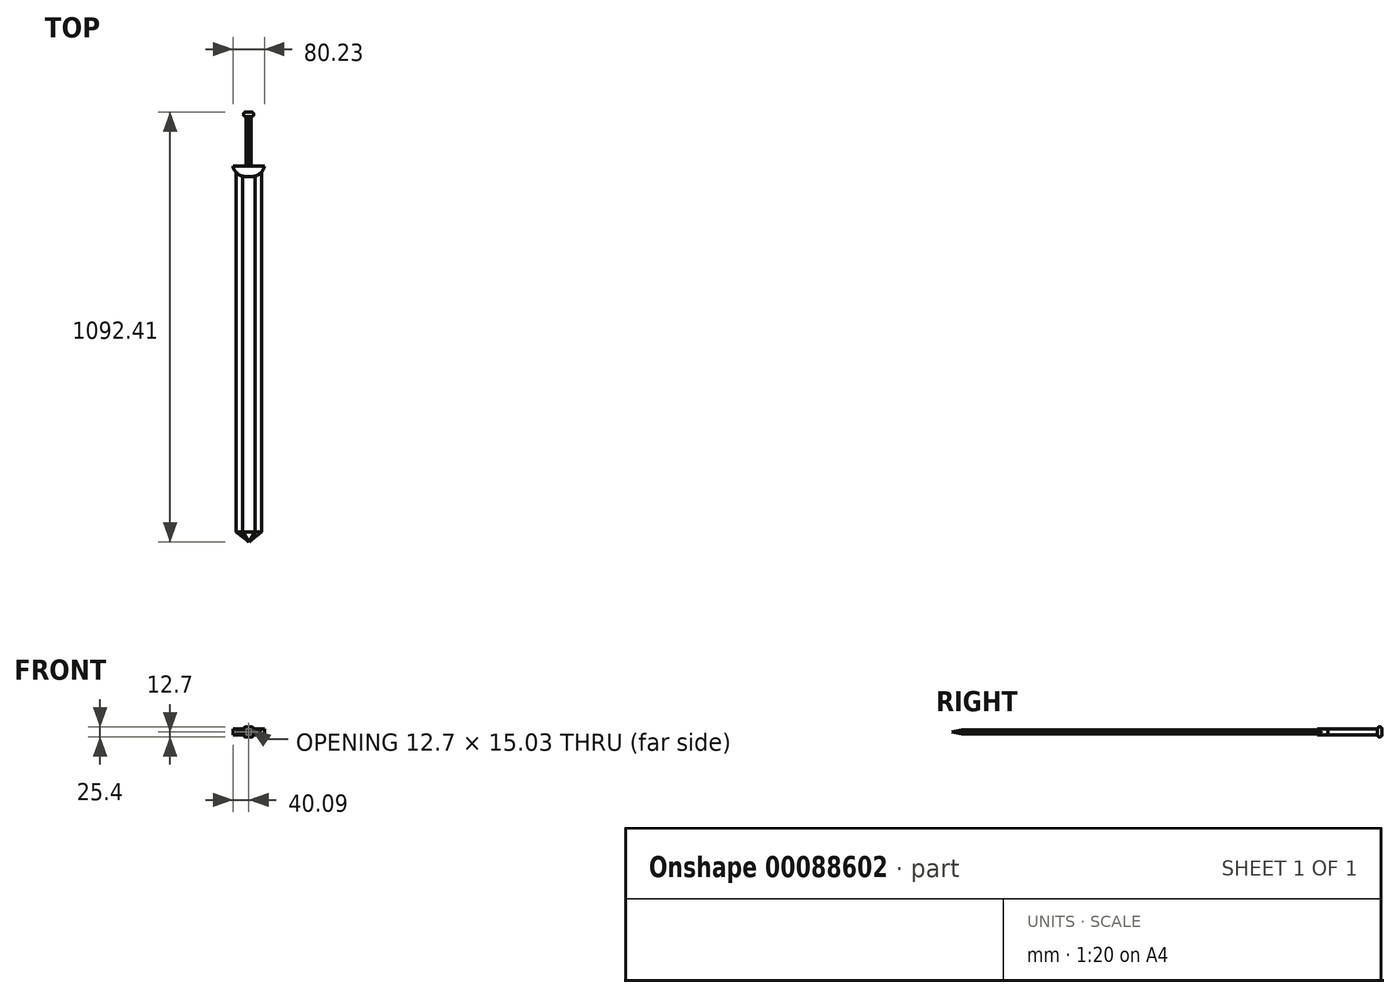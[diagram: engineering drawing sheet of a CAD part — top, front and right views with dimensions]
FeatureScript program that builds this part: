
annotation { "Feature Type Name" : "Feature", "Feature Type Description" : "" }
export const myFeature = defineFeature(function(context is Context, id is Id, definition is map)
    precondition{}
    {
        {
            var Q0;
            Q0=qCreatedBy(makeId("Right.planeOp"),FACE);
            var sketch = newSketch(context, id + "F0", { "sketchPlane" : qUnion([Q0])});
            skLineSegment(sketch, "E0.bottom", {"start": v(0, 0) * mm, "end": v(152.4, 0) * mm});
            skLineSegment(sketch, "E0.top", {"start": v(0, -15.24) * mm, "end": v(152.4, -15.24) * mm});
            skLineSegment(sketch, "E0.left", {"start": v(0, 0) * mm, "end": v(0, -15.24) * mm});
            skLineSegment(sketch, "E0.right", {"start": v(152.4, 0) * mm, "end": v(152.4, -15.24) * mm});
            skSolve(sketch);
        }
        {
            var Q0;
            Q0 = qSketchRegion(id + "F0", true);
            extrude(context, id + "F1", {"entities" : qUnion([Q0]), "depth" : 12.7 * mm});
        }
        {
            var Q0;
            Q0=makeQuery(id+"F1.opExtrude","CAP_EDGE",EDGE,{"disambiguationData":[OSD([sQuery(id+"F0.wireOp",EDGE,"E0.bottom")])],"isStart":true});
            var Q1;
            Q1=makeQuery(id+"F1.opExtrude","CAP_EDGE",EDGE,{"disambiguationData":[OSD([sQuery(id+"F0.wireOp",EDGE,"E0.top")])],"isStart":true});
            var Q2;
            Q2=makeQuery(id+"F1.opExtrude","CAP_EDGE",EDGE,{"disambiguationData":[OSD([sQuery(id+"F0.wireOp",EDGE,"E0.bottom")])],"isStart":false});
            var Q3;
            Q3=makeQuery(id+"F1.opExtrude","CAP_EDGE",EDGE,{"disambiguationData":[OSD([sQuery(id+"F0.wireOp",EDGE,"E0.top")])],"isStart":false});
            fillet(context, id + "F2", {"entities" : qUnion([Q0, Q1, Q2, Q3]), "radius" : 7.62 * mm, "tangentPropagation" : true, "allowEdgeOverflow" : false});
        }
        {
            var Q0;
            Q0=qCreatedBy(makeId("Top.planeOp"),FACE);
            cPlane(context, id + "F3", {"entities" : qUnion([Q0]), "cplaneType" : CPlaneType.OFFSET, "offset" : 7.62 * mm, "oppositeDirection" : true, "width" : 152.4 * mm, "height" : 152.4 * mm});
        }
        {
            var Q0;
            Q0=qCreatedBy(id+"F3.planeOp",FACE);
            var sketch = newSketch(context, id + "F4", { "sketchPlane" : qUnion([Q0])});
            skLineSegment(sketch, "E1.bottom", {"start": v(18.55, 152.06) * mm, "end": v(-6.52, 152.06) * mm});
            skLineSegment(sketch, "E1.top", {"start": v(18.55, 163.8) * mm, "end": v(-6.52, 163.8) * mm});
            skLineSegment(sketch, "E1.left", {"start": v(18.55, 152.06) * mm, "end": v(18.55, 163.8) * mm});
            skLineSegment(sketch, "E1.right", {"start": v(-6.52, 152.06) * mm, "end": v(-6.52, 163.8) * mm});
            skSolve(sketch);
        }
        {
            var Q0;
            Q0 = qSketchRegion(id + "F4", true);
            extrude(context, id + "F5", {"entities" : qUnion([Q0]), "operationType" : NewBodyOperationType.ADD, "depth" : 12.7 * mm, "hasSecondDirection" : true, "secondDirectionOppositeDirection" : true, "secondDirectionDepth" : 12.7 * mm});
        }
        {
            var Q0;
            Q0=qCreatedBy(id+"F3.planeOp",FACE);
            var sketch = newSketch(context, id + "F6", { "sketchPlane" : qUnion([Q0])});
            skArc(sketch, "E2", {"start": v(12.58, -0.66) * mm, "mid": v(34.22, 6.89) * mm, "end": v(46.5, 26.25) * mm});
            skLineSegment(sketch, "E3", {"start": v(12.58, -0.66) * mm, "end": v(0.2, -0.66) * mm});
            skLineSegment(sketch, "E4", {"start": v(6.39, -0.66) * mm, "end": v(6.39, 36.48) * mm});
            skLineSegment(sketch, "E5", {"start": v(46.5, 26.25) * mm, "end": v(6.39, 26.25) * mm});
            skLineSegment(sketch, "E6", {"start": v(6.39, 26.25) * mm, "end": v(-33.74, 26.25) * mm});
            skArc(sketch, "E7", {"start": v(-33.74, 26.25) * mm, "mid": v(-21.46, 6.88) * mm, "end": v(0.2, -0.66) * mm});
            skSolve(sketch);
        }
        {
            var Q0;
            Q0 = qSketchRegion(id + "F6", true);
            extrude(context, id + "F7", {"entities" : qUnion([Q0]), "operationType" : NewBodyOperationType.ADD, "depth" : 7.62 * mm, "hasSecondDirection" : true, "secondDirectionOppositeDirection" : true, "secondDirectionDepth" : 7.62 * mm});
        }
        {
            var Q0;
            Q0=qCreatedBy(id+"F3.planeOp",FACE);
            var sketch = newSketch(context, id + "F8", { "sketchPlane" : qUnion([Q0])});
            skLineSegment(sketch, "E8.bottom", {"start": v(-26.26, 11.18) * mm, "end": v(39.35, 11.18) * mm});
            skLineSegment(sketch, "E8.top", {"start": v(-26.26, -903.22) * mm, "end": v(39.35, -903.22) * mm});
            skLineSegment(sketch, "E8.left", {"start": v(-26.26, 11.18) * mm, "end": v(-26.26, -903.22) * mm});
            skLineSegment(sketch, "E8.right", {"start": v(39.35, 11.18) * mm, "end": v(39.35, -903.22) * mm});
            skSolve(sketch);
        }
        {
            var Q0;
            Q0 = qSketchRegion(id + "F8", true);
            extrude(context, id + "F9", {"entities" : qUnion([Q0]), "operationType" : NewBodyOperationType.ADD, "oppositeDirection" : true, "depth" : 5.08 * mm, "hasSecondDirection" : true, "secondDirectionOppositeDirection" : false, "secondDirectionDepth" : 5.08 * mm});
        }
        {
            var Q0;
            Q0=makeQuery(id+"F9.opExtrude","SWEPT_FACE",FACE,{"disambiguationData":[OSD([sQuery(id+"F8.wireOp",EDGE,"E8.top")])]});
            var sketch = newSketch(context, id + "F10", { "sketchPlane" : qUnion([Q0])});
            skLineSegment(sketch, "E9", {"start": v(-26.26, -7.62) * mm, "end": v(-9.22, -2.54) * mm});
            skLineSegment(sketch, "E10", {"start": v(-26.26, -7.62) * mm, "end": v(-9.22, -12.7) * mm});
            skLineSegment(sketch, "E11", {"start": v(39.35, -7.62) * mm, "end": v(22.3, -2.54) * mm});
            skLineSegment(sketch, "E12", {"start": v(39.35, -7.62) * mm, "end": v(22.3, -12.7) * mm});
            skSolve(sketch);
        }
        {
            var Q0;
            Q0 = qSketchRegion(id + "F10", true);
            var Q1;
            {var subQ0=sQuery(id+"F10.wireOp",EDGE,"E9");Q1=makeQuery(id+"F10.imprint","IMPRINT",FACE,{"disambiguationData":[TD([[makeQuery(id+"F10.imprint","IMPRINT",EDGE,{"derivedFrom":subQ0}),1.0]])]});}
            var Q2;
            {var subQ0=sQuery(id+"F10.wireOp",EDGE,"E10");Q2=makeQuery(id+"F10.imprint","IMPRINT",FACE,{"disambiguationData":[TD([[makeQuery(id+"F10.imprint","IMPRINT",EDGE,{"derivedFrom":subQ0}),-1.0]])]});}
            var Q3;
            {var subQ0=sQuery(id+"F10.wireOp",EDGE,"E12");Q3=makeQuery(id+"F10.imprint","IMPRINT",FACE,{"disambiguationData":[TD([[makeQuery(id+"F10.imprint","IMPRINT",EDGE,{"derivedFrom":subQ0}),1.0]])]});}
            var Q4;
            {var subQ0=sQuery(id+"F10.wireOp",EDGE,"E11");Q4=makeQuery(id+"F10.imprint","IMPRINT",FACE,{"disambiguationData":[TD([[makeQuery(id+"F10.imprint","IMPRINT",EDGE,{"derivedFrom":subQ0}),-1.0]])]});}
            extrude(context, id + "F11", {"entities" : qUnion([Q0, Q1, Q2, Q3, Q4]), "operationType" : NewBodyOperationType.REMOVE, "oppositeDirection" : true, "depth" : 914.4 * mm});
        }
        {
            var Q0;
            Q0=makeQuery(id+"F7.opExtrude","CAP_FACE",FACE,{"disambiguationData":[OSD([sQuery(id+"F6.wireOp",EDGE,"E2"),sQuery(id+"F6.wireOp",EDGE,"E3"),sQuery(id+"F6.wireOp",EDGE,"E5"),sQuery(id+"F6.wireOp",EDGE,"E6"),sQuery(id+"F6.wireOp",EDGE,"E7")])],"isStart":false});
            extrude(context, id + "F12", {"entities" : qUnion([Q0]), "operationType" : NewBodyOperationType.ADD, "oppositeDirection" : true, "depth" : 12.7 * mm});
        }
        {
            var Q0;
            Q0=makeQuery(id+"F9.opExtrude","SWEPT_FACE",FACE,{"disambiguationData":[OSD([sQuery(id+"F8.wireOp",EDGE,"E8.top")])]});
            cPlane(context, id + "F13", {"entities" : qUnion([Q0]), "cplaneType" : CPlaneType.OFFSET, "offset" : 25.4 * mm, "width" : 152.4 * mm, "height" : 152.4 * mm});
        }
        {
            var Q0;
            Q0=qCreatedBy(id+"F13.planeOp",FACE);
            var sketch = newSketch(context, id + "F14", { "sketchPlane" : qUnion([Q0])});
            skPoint(sketch, "E13", {"position": v(6.65, -7.57) * mm});
            skSolve(sketch);
        }
        {
            var Q1;
            Q1=makeQuery(id+"F9.opExtrude","SWEPT_FACE",FACE,{"disambiguationData":[OSD([sQuery(id+"F8.wireOp",EDGE,"E8.top")])]});
            var Q2;
            Q2=sQuery(id+"F14.wireOp",VERTEX,"E13");
            loft(context, id + "F15", {"operationType" : NewBodyOperationType.ADD, "sheetProfilesArray" : [{ "sheetProfileEntities" : qUnion([Q1]) }, { "sheetProfileEntities" : qUnion([Q2]) }]});
        }
        {
            var Q0;
            Q0=makeQuery(id+"F5.opExtrude","SWEPT_FACE",FACE,{"disambiguationData":[OSD([sQuery(id+"F4.wireOp",EDGE,"E1.right")])]});
            var Q1;
            Q1=makeQuery(id+"F5.opExtrude","CAP_FACE",FACE,{"disambiguationData":[OSD([sQuery(id+"F4.wireOp",EDGE,"E1.bottom"),sQuery(id+"F4.wireOp",EDGE,"E1.top"),sQuery(id+"F4.wireOp",EDGE,"E1.left"),sQuery(id+"F4.wireOp",EDGE,"E1.right")])],"isStart":false});
            var Q2;
            Q2=makeQuery(id+"F5.opExtrude","SWEPT_FACE",FACE,{"disambiguationData":[OSD([sQuery(id+"F4.wireOp",EDGE,"E1.left")])]});
            var Q3;
            Q3=makeQuery(id+"F5.opExtrude","CAP_FACE",FACE,{"disambiguationData":[OSD([sQuery(id+"F4.wireOp",EDGE,"E1.bottom"),sQuery(id+"F4.wireOp",EDGE,"E1.top"),sQuery(id+"F4.wireOp",EDGE,"E1.left"),sQuery(id+"F4.wireOp",EDGE,"E1.right")])],"isStart":true});
            fillet(context, id + "F16", {"entities" : qUnion([Q0, Q1, Q2, Q3]), "radius" : 5.08 * mm, "tangentPropagation" : true, "allowEdgeOverflow" : false});
        }
    });
